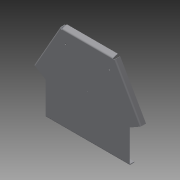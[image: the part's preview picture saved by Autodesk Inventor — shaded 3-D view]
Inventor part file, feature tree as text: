
AUTODESK INVENTOR PART (.ipt)
format: ipt  version: 2014 SP2 (Build 180246200, 246)  size: 208,896 bytes
history: native  units: mm
features: other x4, sketch x3, extrude x1
ambient origin geometry x8: Origin, YZ Plane, XZ Plane, XY Plane, X Axis, Y Axis, Z Axis, Center Point
bodies: Solid1 (feature_tree)
feature tree (8):
  extrude  "Extrusion1"  Depth=50.0mm
  other  "Bend Part1"
  other  "Bend Part5"
  other  "Bend Part6"
  other  "Bend Part7"
  sketch  "Sketch1"  dims[d0=254.0mm d2=50.0mm d6=32.5mm d12=32.5mm]
  sketch  "Sketch10"  dims[d13=50.0mm]
  sketch  "Sketch11"  dims[d14=35.0mm d15=20.0mm d16=10.0mm d17=0.0mm d18=105.0mm d31=3.0mm d32=0.0mm d33=8.0mm d34=3.0mm d64=145.0mm d65=50.0mm d66=35.0mm d67=20.0mm d68=10.0mm d69=0.0mm d70=8.0mm d71=105.0mm d72=145.0mm d82=24.0mm d85=3.0mm d86=12.740904mm d153=25.0mm d162=3.0mm d163=90.0deg d165=3.0mm d166=90.0deg d168=3.0mm d169=90.0deg d210=443.0mm d212=122.0mm d215=175.0mm d217=45.309788mm d218=25.713207mm d220=217.286793mm d222=24.0mm d223=24.0mm d224=24.0mm d226=24.0mm d227=30.0mm d228=30.0mm d233=300.0mm]
